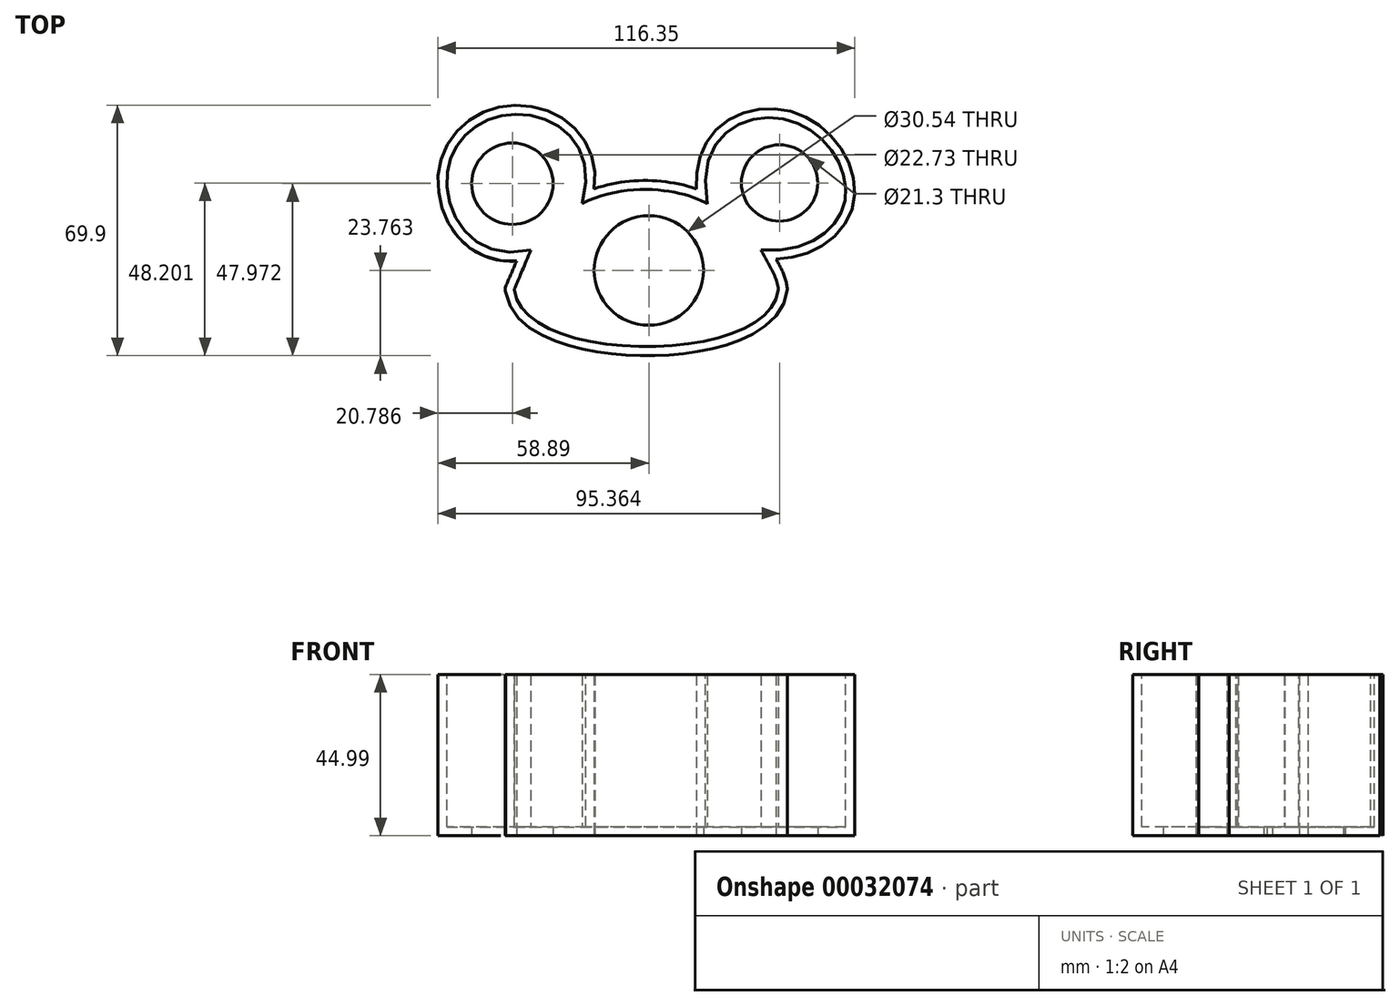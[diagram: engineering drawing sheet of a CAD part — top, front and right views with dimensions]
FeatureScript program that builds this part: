
annotation { "Feature Type Name" : "Feature", "Feature Type Description" : "" }
export const myFeature = defineFeature(function(context is Context, id is Id, definition is map)
    precondition{}
    {
        {
            var Q0;
            Q0=qCreatedBy(makeId("Top.planeOp"),FACE);
            var sketch = newSketch(context, id + "F0", { "sketchPlane" : qUnion([Q0])});
            skFitSpline(sketch, "E0", {"points": [v(-18.66, 7.74) * mm, v(-36.6, 32.67) * mm, v(-56.23, 16.45) * mm, v(-32.95, -5.22) * mm], "startDerivative": vector(41.92, 145.23) * mm, "endDerivative": vector(145.08, 34.05) * mm});
            skFitSpline(sketch, "E1", {"points": [v(-32.95, -5.22) * mm, v(-37.53, -16.12) * mm, v(-37.53, -16.3) * mm], "startDerivative": vector(-7.26, -18.12) * mm, "endDerivative": vector(1.94, 0.67) * mm});
            skFitSpline(sketch, "E2", {"points": [v(-37.53, -16.3) * mm, v(0, -32.23) * mm, v(36.16, -16.3) * mm], "startDerivative": vector(6.09, -63.9) * mm, "endDerivative": vector(7.25, 63.16) * mm});
            skFitSpline(sketch, "E3", {"points": [v(36.16, -16.3) * mm, v(31.33, -5.27) * mm], "startDerivative": vector(-1, 11.65) * mm, "endDerivative": vector(-4.76, 10.52) * mm});
            skFitSpline(sketch, "E4", {"points": [v(31.33, -5.27) * mm, v(54.95, 10.64) * mm, v(37.7, 31.3) * mm, v(16.35, 7.56) * mm], "startDerivative": vector(132.77, -8) * mm, "endDerivative": vector(31.85, -165.05) * mm});
            skFitSpline(sketch, "E5", {"points": [v(16.35, 7.56) * mm, v(-18.66, 7.74) * mm], "startDerivative": vector(-17.93, 11.27) * mm, "endDerivative": vector(-41, -19.98) * mm});
            skSolve(sketch);
        }
        {
            var Q0;
            Q0=makeQuery(id+"F0.imprint","IMPRINT",FACE,{"disambiguationData":[TD([[makeQuery(id+"F0.imprint","IMPRINT",EDGE,{"derivedFrom":sQuery(id+"F0.wireOp",EDGE,"E0")}),1.0]])]});
            extrude(context, id + "F1", {"entities" : qUnion([Q0]), "depth" : 42.5 * mm});
        }
        {
            var Q0;
            Q0=makeQuery(id+"F1.opExtrude","CAP_FACE",FACE,{"disambiguationData":[OSD([sQuery(id+"F0.wireOp",EDGE,"E0"),sQuery(id+"F0.wireOp",EDGE,"E1"),sQuery(id+"F0.wireOp",EDGE,"E2"),sQuery(id+"F0.wireOp",EDGE,"E3"),sQuery(id+"F0.wireOp",EDGE,"E4"),sQuery(id+"F0.wireOp",EDGE,"E5")])],"isStart":false});
            shell(context, id + "F2", {"entities" : qUnion([Q0]), "thickness" : 2.5 * mm, "oppositeDirection" : true});
        }
        {
            var Q0;
            Q0=makeQuery(id+"F1.opExtrude","CAP_FACE",FACE,{"disambiguationData":[OSD([sQuery(id+"F0.wireOp",EDGE,"E0"),sQuery(id+"F0.wireOp",EDGE,"E1"),sQuery(id+"F0.wireOp",EDGE,"E2"),sQuery(id+"F0.wireOp",EDGE,"E3"),sQuery(id+"F0.wireOp",EDGE,"E4"),sQuery(id+"F0.wireOp",EDGE,"E5")])],"isStart":true});
            var sketch = newSketch(context, id + "F3", { "sketchPlane" : qUnion([Q0])});
            skCircle(sketch, "E6", {"center": v(0, 10.97) * mm, "radius": 15.27 * mm});
            skSolve(sketch);
        }
        {
            var Q0;
            Q0=makeQuery(id+"F3.imprint","IMPRINT",FACE,{"disambiguationData":[TD([[makeQuery(id+"F3.imprint","IMPRINT",EDGE,{"derivedFrom":sQuery(id+"F3.wireOp",EDGE,"E6")}),1.0]])]});
            extrude(context, id + "F4", {"entities" : qUnion([Q0]), "operationType" : NewBodyOperationType.REMOVE, "oppositeDirection" : true, "depth" : 82.92 * mm});
        }
        {
            var Q0;
            Q0=makeQuery(id+"F3.imprint","IMPRINT",FACE,{"disambiguationData":[TD([[makeQuery(id+"F3.imprint","IMPRINT",EDGE,{"derivedFrom":sQuery(id+"F3.wireOp",EDGE,"E6")}),-1.0]])]});
            var sketch = newSketch(context, id + "F5", { "sketchPlane" : qUnion([Q0])});
            skCircle(sketch, "E7", {"center": v(36.47, -13.47) * mm, "radius": 10.65 * mm});
            skCircle(sketch, "E8", {"center": v(-38.1, -13.24) * mm, "radius": 11.37 * mm});
            skSolve(sketch);
        }
        {
            var Q0;
            Q0 = qSketchRegion(id + "F5", true);
            extrude(context, id + "F6", {"entities" : qUnion([Q0]), "operationType" : NewBodyOperationType.REMOVE, "oppositeDirection" : true, "depth" : 78.75 * mm});
        }
    });
